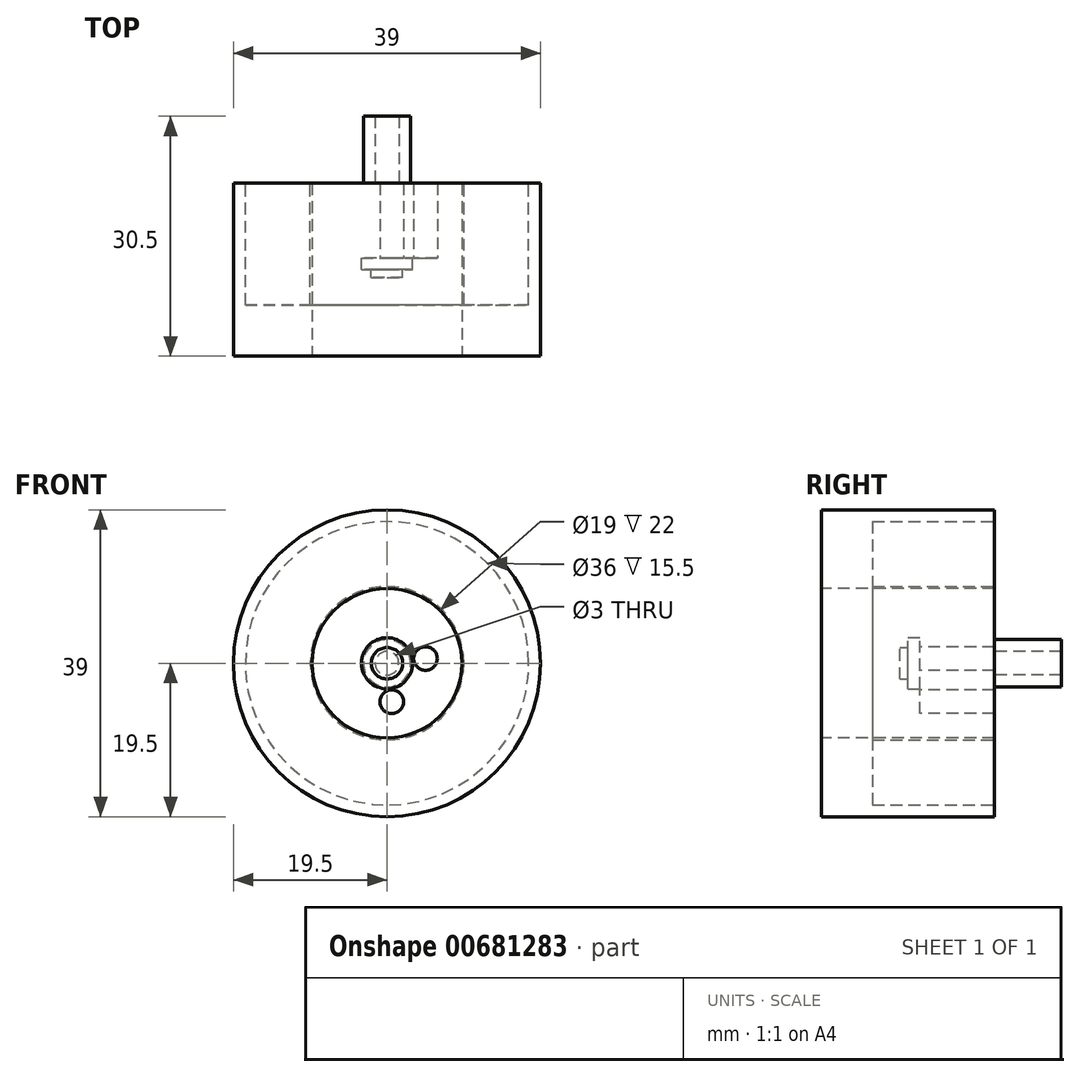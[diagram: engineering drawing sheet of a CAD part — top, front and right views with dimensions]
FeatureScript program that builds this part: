
annotation { "Feature Type Name" : "Feature", "Feature Type Description" : "" }
export const myFeature = defineFeature(function(context is Context, id is Id, definition is map)
    precondition{}
    {
        {
            var Q0;
            Q0=qCreatedBy(makeId("Front.planeOp"),FACE);
            var sketch = newSketch(context, id + "F0", { "sketchPlane" : qUnion([Q0])});
            skCircle(sketch, "E0", {"center": v(0, 0) * mm, "radius": 19.5 * mm});
            skCircle(sketch, "E1", {"center": v(0, 0) * mm, "radius": 9.5 * mm});
            skSolve(sketch);
        }
        {
            var Q0;
            Q0=qSketchRegion(id+"F0",true);
            var Q1;
            Q1=makeQuery(id+"F0.imprint","IMPRINT",FACE,{"disambiguationData":[TD([[makeQuery(id+"F0.imprint","IMPRINT",EDGE,{"derivedFrom":sQuery(id+"F0.wireOp",EDGE,"E1")}),1.0]])]});
            extrude(context, id + "F1", {"entities" : qUnion([Q0, Q1]), "oppositeDirection" : true, "depth" : 22 * mm, "offsetDistance" : 25.4 * mm});
        }
        {
            var Q0;
            Q0=makeQuery(id+"F0.imprint","IMPRINT",FACE,{"disambiguationData":[TD([[makeQuery(id+"F0.imprint","IMPRINT",EDGE,{"derivedFrom":sQuery(id+"F0.wireOp",EDGE,"E1")}),1.0]])]});
            extrude(context, id + "F2", {"entities" : qUnion([Q0]), "operationType" : NewBodyOperationType.REMOVE, "oppositeDirection" : true, "depth" : 12.5 * mm, "offsetDistance" : 25.4 * mm});
        }
        {
            var Q0;
            Q0=makeQuery(id+"F2.boolean.opBoolean","COPY",FACE,{"derivedFrom":makeQuery(id+"F2.opExtrude","CAP_FACE",FACE,{"disambiguationData":[OSD([sQuery(id+"F0.wireOp",EDGE,"E1")])],"isStart":false})});
            var sketch = newSketch(context, id + "F3", { "sketchPlane" : qUnion([Q0])});
            skCircle(sketch, "E2", {"center": v(0, 0) * mm, "radius": 4.92 * mm});
            skCircle(sketch, "E3", {"center": v(-0.6, 4.89) * mm, "radius": 1.5 * mm});
            skCircle(sketch, "E4.1.0", {"center": v(-3.88, 3.03) * mm, "radius": 1.5 * mm});
            skCircle(sketch, "E4.2.0", {"center": v(-4.89, -0.6) * mm, "radius": 1.5 * mm});
            skCircle(sketch, "E4.3.0", {"center": v(-3.03, -3.88) * mm, "radius": 1.5 * mm});
            skCircle(sketch, "E4.4.0", {"center": v(0.6, -4.89) * mm, "radius": 1.5 * mm});
            skCircle(sketch, "E4.5.0", {"center": v(3.88, -3.03) * mm, "radius": 1.5 * mm});
            skCircle(sketch, "E4.6.0", {"center": v(4.89, 0.6) * mm, "radius": 1.5 * mm});
            skCircle(sketch, "E4.7.0", {"center": v(3.03, 3.88) * mm, "radius": 1.5 * mm});
            skSolve(sketch);
        }
        {
            var Q0;
            {var subQ0=sQuery(id+"F3.wireOp",EDGE,"E4.7.0");var subQ1=sQuery(id+"F3.wireOp",EDGE,"E2");var subQ2=makeQuery(id+"F3.imprint","INTERSECT",VERTEX,{"disambiguationData":[OD(0.0)],"derivedFrom":[subQ1,subQ0]});Q0=makeQuery(id+"F3.imprint","IMPRINT",FACE,{"disambiguationData":[TD([[makeQuery(id+"F3.imprint","IMPRINT",EDGE,{"disambiguationData":[TD([[subQ2,-1.0]])],"derivedFrom":subQ1}),1.0]])]});}
            var Q1;
            {var subQ0=sQuery(id+"F3.wireOp",EDGE,"E4.7.0");var subQ1=sQuery(id+"F3.wireOp",EDGE,"E2");var subQ2=makeQuery(id+"F3.imprint","INTERSECT",VERTEX,{"disambiguationData":[OD(0.0)],"derivedFrom":[subQ1,subQ0]});Q1=makeQuery(id+"F3.imprint","IMPRINT",FACE,{"disambiguationData":[TD([[makeQuery(id+"F3.imprint","IMPRINT",EDGE,{"disambiguationData":[TD([[subQ2,-1.0]])],"derivedFrom":subQ1}),-1.0]])]});}
            var Q2;
            {var subQ0=sQuery(id+"F3.wireOp",EDGE,"E3");var subQ1=sQuery(id+"F3.wireOp",EDGE,"E2");var subQ2=makeQuery(id+"F3.imprint","INTERSECT",VERTEX,{"disambiguationData":[OD(0.0)],"derivedFrom":[subQ1,subQ0]});Q2=makeQuery(id+"F3.imprint","IMPRINT",FACE,{"disambiguationData":[TD([[makeQuery(id+"F3.imprint","IMPRINT",EDGE,{"disambiguationData":[TD([[subQ2,-1.0]])],"derivedFrom":subQ1}),1.0]])]});}
            var Q3;
            {var subQ0=sQuery(id+"F3.wireOp",EDGE,"E3");var subQ1=sQuery(id+"F3.wireOp",EDGE,"E2");var subQ2=makeQuery(id+"F3.imprint","INTERSECT",VERTEX,{"disambiguationData":[OD(0.0)],"derivedFrom":[subQ1,subQ0]});Q3=makeQuery(id+"F3.imprint","IMPRINT",FACE,{"disambiguationData":[TD([[makeQuery(id+"F3.imprint","IMPRINT",EDGE,{"disambiguationData":[TD([[subQ2,-1.0]])],"derivedFrom":subQ1}),-1.0]])]});}
            var Q4;
            {var subQ0=sQuery(id+"F3.wireOp",EDGE,"E4.1.0");var subQ1=sQuery(id+"F3.wireOp",EDGE,"E2");var subQ2=makeQuery(id+"F3.imprint","INTERSECT",VERTEX,{"disambiguationData":[OD(0.0)],"derivedFrom":[subQ1,subQ0]});Q4=makeQuery(id+"F3.imprint","IMPRINT",FACE,{"disambiguationData":[TD([[makeQuery(id+"F3.imprint","IMPRINT",EDGE,{"disambiguationData":[TD([[subQ2,-1.0]])],"derivedFrom":subQ1}),1.0]])]});}
            var Q5;
            {var subQ0=sQuery(id+"F3.wireOp",EDGE,"E4.1.0");var subQ1=sQuery(id+"F3.wireOp",EDGE,"E2");var subQ2=makeQuery(id+"F3.imprint","INTERSECT",VERTEX,{"disambiguationData":[OD(0.0)],"derivedFrom":[subQ1,subQ0]});Q5=makeQuery(id+"F3.imprint","IMPRINT",FACE,{"disambiguationData":[TD([[makeQuery(id+"F3.imprint","IMPRINT",EDGE,{"disambiguationData":[TD([[subQ2,-1.0]])],"derivedFrom":subQ1}),-1.0]])]});}
            var Q6;
            {var subQ0=sQuery(id+"F3.wireOp",EDGE,"E4.2.0");var subQ1=sQuery(id+"F3.wireOp",EDGE,"E2");var subQ2=makeQuery(id+"F3.imprint","INTERSECT",VERTEX,{"disambiguationData":[OD(0.0)],"derivedFrom":[subQ1,subQ0]});Q6=makeQuery(id+"F3.imprint","IMPRINT",FACE,{"disambiguationData":[TD([[makeQuery(id+"F3.imprint","IMPRINT",EDGE,{"disambiguationData":[TD([[subQ2,-1.0]])],"derivedFrom":subQ1}),1.0]])]});}
            var Q7;
            {var subQ0=sQuery(id+"F3.wireOp",EDGE,"E4.2.0");var subQ1=sQuery(id+"F3.wireOp",EDGE,"E2");var subQ2=makeQuery(id+"F3.imprint","INTERSECT",VERTEX,{"disambiguationData":[OD(0.0)],"derivedFrom":[subQ1,subQ0]});Q7=makeQuery(id+"F3.imprint","IMPRINT",FACE,{"disambiguationData":[TD([[makeQuery(id+"F3.imprint","IMPRINT",EDGE,{"disambiguationData":[TD([[subQ2,-1.0]])],"derivedFrom":subQ1}),-1.0]])]});}
            var Q8;
            {var subQ0=sQuery(id+"F3.wireOp",EDGE,"E4.3.0");var subQ1=sQuery(id+"F3.wireOp",EDGE,"E2");var subQ2=makeQuery(id+"F3.imprint","INTERSECT",VERTEX,{"disambiguationData":[OD(0.0)],"derivedFrom":[subQ1,subQ0]});Q8=makeQuery(id+"F3.imprint","IMPRINT",FACE,{"disambiguationData":[TD([[makeQuery(id+"F3.imprint","IMPRINT",EDGE,{"disambiguationData":[TD([[subQ2,-1.0]])],"derivedFrom":subQ1}),1.0]])]});}
            var Q9;
            {var subQ0=sQuery(id+"F3.wireOp",EDGE,"E4.3.0");var subQ1=sQuery(id+"F3.wireOp",EDGE,"E2");var subQ2=makeQuery(id+"F3.imprint","INTERSECT",VERTEX,{"disambiguationData":[OD(0.0)],"derivedFrom":[subQ1,subQ0]});Q9=makeQuery(id+"F3.imprint","IMPRINT",FACE,{"disambiguationData":[TD([[makeQuery(id+"F3.imprint","IMPRINT",EDGE,{"disambiguationData":[TD([[subQ2,-1.0]])],"derivedFrom":subQ1}),-1.0]])]});}
            var Q10;
            {var subQ0=sQuery(id+"F3.wireOp",EDGE,"E4.4.0");var subQ1=sQuery(id+"F3.wireOp",EDGE,"E2");var subQ2=makeQuery(id+"F3.imprint","INTERSECT",VERTEX,{"disambiguationData":[OD(0.0)],"derivedFrom":[subQ1,subQ0]});Q10=makeQuery(id+"F3.imprint","IMPRINT",FACE,{"disambiguationData":[TD([[makeQuery(id+"F3.imprint","IMPRINT",EDGE,{"disambiguationData":[TD([[subQ2,-1.0]])],"derivedFrom":subQ1}),1.0]])]});}
            var Q11;
            {var subQ0=sQuery(id+"F3.wireOp",EDGE,"E4.4.0");var subQ1=sQuery(id+"F3.wireOp",EDGE,"E2");var subQ2=makeQuery(id+"F3.imprint","INTERSECT",VERTEX,{"disambiguationData":[OD(0.0)],"derivedFrom":[subQ1,subQ0]});Q11=makeQuery(id+"F3.imprint","IMPRINT",FACE,{"disambiguationData":[TD([[makeQuery(id+"F3.imprint","IMPRINT",EDGE,{"disambiguationData":[TD([[subQ2,-1.0]])],"derivedFrom":subQ1}),-1.0]])]});}
            var Q12;
            {var subQ0=sQuery(id+"F3.wireOp",EDGE,"E4.5.0");var subQ1=sQuery(id+"F3.wireOp",EDGE,"E2");var subQ2=makeQuery(id+"F3.imprint","INTERSECT",VERTEX,{"disambiguationData":[OD(0.0)],"derivedFrom":[subQ1,subQ0]});Q12=makeQuery(id+"F3.imprint","IMPRINT",FACE,{"disambiguationData":[TD([[makeQuery(id+"F3.imprint","IMPRINT",EDGE,{"disambiguationData":[TD([[subQ2,-1.0]])],"derivedFrom":subQ1}),1.0]])]});}
            var Q13;
            {var subQ0=sQuery(id+"F3.wireOp",EDGE,"E4.5.0");var subQ1=sQuery(id+"F3.wireOp",EDGE,"E2");var subQ2=makeQuery(id+"F3.imprint","INTERSECT",VERTEX,{"disambiguationData":[OD(0.0)],"derivedFrom":[subQ1,subQ0]});Q13=makeQuery(id+"F3.imprint","IMPRINT",FACE,{"disambiguationData":[TD([[makeQuery(id+"F3.imprint","IMPRINT",EDGE,{"disambiguationData":[TD([[subQ2,-1.0]])],"derivedFrom":subQ1}),-1.0]])]});}
            var Q14;
            {var subQ0=sQuery(id+"F3.wireOp",EDGE,"E4.6.0");var subQ1=sQuery(id+"F3.wireOp",EDGE,"E2");var subQ2=makeQuery(id+"F3.imprint","INTERSECT",VERTEX,{"disambiguationData":[OD(0.0)],"derivedFrom":[subQ1,subQ0]});Q14=makeQuery(id+"F3.imprint","IMPRINT",FACE,{"disambiguationData":[TD([[makeQuery(id+"F3.imprint","IMPRINT",EDGE,{"disambiguationData":[TD([[subQ2,1.0]])],"derivedFrom":subQ1}),1.0]])]});}
            var Q15;
            {var subQ0=sQuery(id+"F3.wireOp",EDGE,"E4.6.0");var subQ1=sQuery(id+"F3.wireOp",EDGE,"E2");var subQ2=makeQuery(id+"F3.imprint","INTERSECT",VERTEX,{"disambiguationData":[OD(0.0)],"derivedFrom":[subQ1,subQ0]});Q15=makeQuery(id+"F3.imprint","IMPRINT",FACE,{"disambiguationData":[TD([[makeQuery(id+"F3.imprint","IMPRINT",EDGE,{"disambiguationData":[TD([[subQ2,1.0]])],"derivedFrom":subQ1}),-1.0]])]});}
            extrude(context, id + "F4", {"entities" : qUnion([Q0, Q1, Q2, Q3, Q4, Q5, Q6, Q7, Q8, Q9, Q10, Q11, Q12, Q13, Q14, Q15]), "operationType" : NewBodyOperationType.REMOVE, "oppositeDirection" : true, "depth" : 25.4 * mm, "offsetDistance" : 25.4 * mm});
        }
        {
            var Q0;
            Q0=makeQuery(id+"F1.opExtrude","CAP_FACE",FACE,{"disambiguationData":[OSD([sQuery(id+"F0.wireOp",EDGE,"E0")])],"isStart":false});
            var sketch = newSketch(context, id + "F5", { "sketchPlane" : qUnion([Q0])});
            skCircle(sketch, "E5", {"center": v(0, 0) * mm, "radius": 1.5 * mm});
            skCircle(sketch, "E6", {"center": v(0, 0) * mm, "radius": 3 * mm});
            skSolve(sketch);
        }
        {
            var Q0;
            Q0=qSketchRegion(id+"F5",true);
            extrude(context, id + "F6", {"entities" : qUnion([Q0]), "operationType" : NewBodyOperationType.ADD, "depth" : 8.5 * mm, "offsetDistance" : 25.4 * mm});
        }
        {
            var Q0;
            {var subQ0=sQuery(id+"F0.wireOp",EDGE,"E0");Q0=makeQuery(id+"F6.boolean.opBoolean","SPLIT",FACE,{"disambiguationData":[TD([makeQuery(id+"F1.opExtrude","SWEPT_FACE",FACE,{"disambiguationData":[OSD([subQ0])]})])],"derivedFrom":makeQuery(id+"F1.opExtrude","CAP_FACE",FACE,{"disambiguationData":[OSD([subQ0])],"isStart":false})});}
            var sketch = newSketch(context, id + "F7", { "sketchPlane" : qUnion([Q0])});
            skCircle(sketch, "E7", {"center": v(0, 0) * mm, "radius": 18 * mm});
            skCircle(sketch, "E8", {"center": v(0, 0) * mm, "radius": 9.75 * mm});
            skSolve(sketch);
        }
        {
            var Q0;
            Q0=makeQuery(id+"F7.imprint","IMPRINT",FACE,{"disambiguationData":[TD([[makeQuery(id+"F7.imprint","IMPRINT",EDGE,{"derivedFrom":sQuery(id+"F7.wireOp",EDGE,"E7")}),1.0]])]});
            extrude(context, id + "F8", {"entities" : qUnion([Q0]), "operationType" : NewBodyOperationType.REMOVE, "oppositeDirection" : true, "depth" : 15.5 * mm, "offsetDistance" : 25.4 * mm});
        }
        {
            var Q0;
            Q0=makeQuery(id+"F2.boolean.opBoolean","COPY",FACE,{"derivedFrom":makeQuery(id+"F2.opExtrude","CAP_FACE",FACE,{"disambiguationData":[OSD([sQuery(id+"F0.wireOp",EDGE,"E1")])],"isStart":false})});
            var sketch = newSketch(context, id + "F9", { "sketchPlane" : qUnion([Q0])});
            skCircle(sketch, "E9", {"center": v(0, 0) * mm, "radius": 3.25 * mm});
            skSolve(sketch);
        }
        {
            var Q0;
            Q0=qSketchRegion(id+"F9",true);
            extrude(context, id + "F10", {"entities" : qUnion([Q0]), "operationType" : NewBodyOperationType.ADD, "depth" : 1.5 * mm, "offsetDistance" : 25.4 * mm});
        }
        {
            var Q0;
            Q0=makeQuery(id+"F10.opExtrude","CAP_FACE",FACE,{"disambiguationData":[OSD([sQuery(id+"F9.wireOp",EDGE,"E9")])],"isStart":false});
            var sketch = newSketch(context, id + "F11", { "sketchPlane" : qUnion([Q0])});
            skCircle(sketch, "E10", {"center": v(0, 0) * mm, "radius": 2 * mm});
            skSolve(sketch);
        }
        {
            var Q0;
            Q0=qSketchRegion(id+"F11",true);
            extrude(context, id + "F12", {"entities" : qUnion([Q0]), "operationType" : NewBodyOperationType.ADD, "depth" : 1 * mm, "offsetDistance" : 25.4 * mm});
        }
    });
